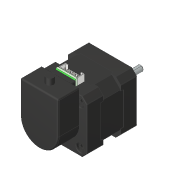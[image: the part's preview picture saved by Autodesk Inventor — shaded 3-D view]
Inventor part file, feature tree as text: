
AUTODESK INVENTOR PART (.ipt)
format: ipt  version: 2018 (Build 220112000, 112)  size: 354,816 bytes
history: native  units: in
note: dims shown in document units (in); Inventor stores cm internally (conversion verified against a paired STEP export)
features: extrude x5, sketch x5, chamfer x1, fillet x1, projected_geometry x1, other x1
ambient origin geometry x8: Origin, YZ Plane, XZ Plane, XY Plane, X Axis, Y Axis, Z Axis, Center Point
bodies: Solid1 (feature_tree)
feature tree (14):
  extrude  "Extrusion1"  Depth=0.3937in TaperAngle=0.0deg
  extrude  "Extrusion2"  Depth=0.0197in TaperAngle=45.0deg
  extrude  "Extrusion3"  Depth=1.0236in
  chamfer  "Chamfer1"  Distance=0.6693in
  extrude  "Extrusion4"  Depth=0.2362in
  fillet  "Fillet1"  Radius=0.1969in
  extrude  "Extrusion5"  [1 undecoded]
  sketch  "Sketch1"  dims[d0=0.3937in d1=0.0in d2=0.3937in d3=0.0in]
  sketch  "Sketch2"  dims[d4=0.0394in d5=0.0in d6=0.0197in d7=0.0787in d8=45.0deg]
  sketch  "Sketch3"  dims[d9=1.1811in d10=1.0236in d11=0.6693in d12=0.0in]
  projected_geometry  "Projected Loop1"
  sketch  "Sketch4"  dims[d13=0.0394in d14=0.2362in d15=0.1969in d16=0.0in]
  sketch  "Sketch5"
  other  "Filete1"
note: 1 required parameter value undecoded (feature->parameter linkage not recoverable at this tier; creation-order binding heuristic only, values carry confidence <= 0.55)
